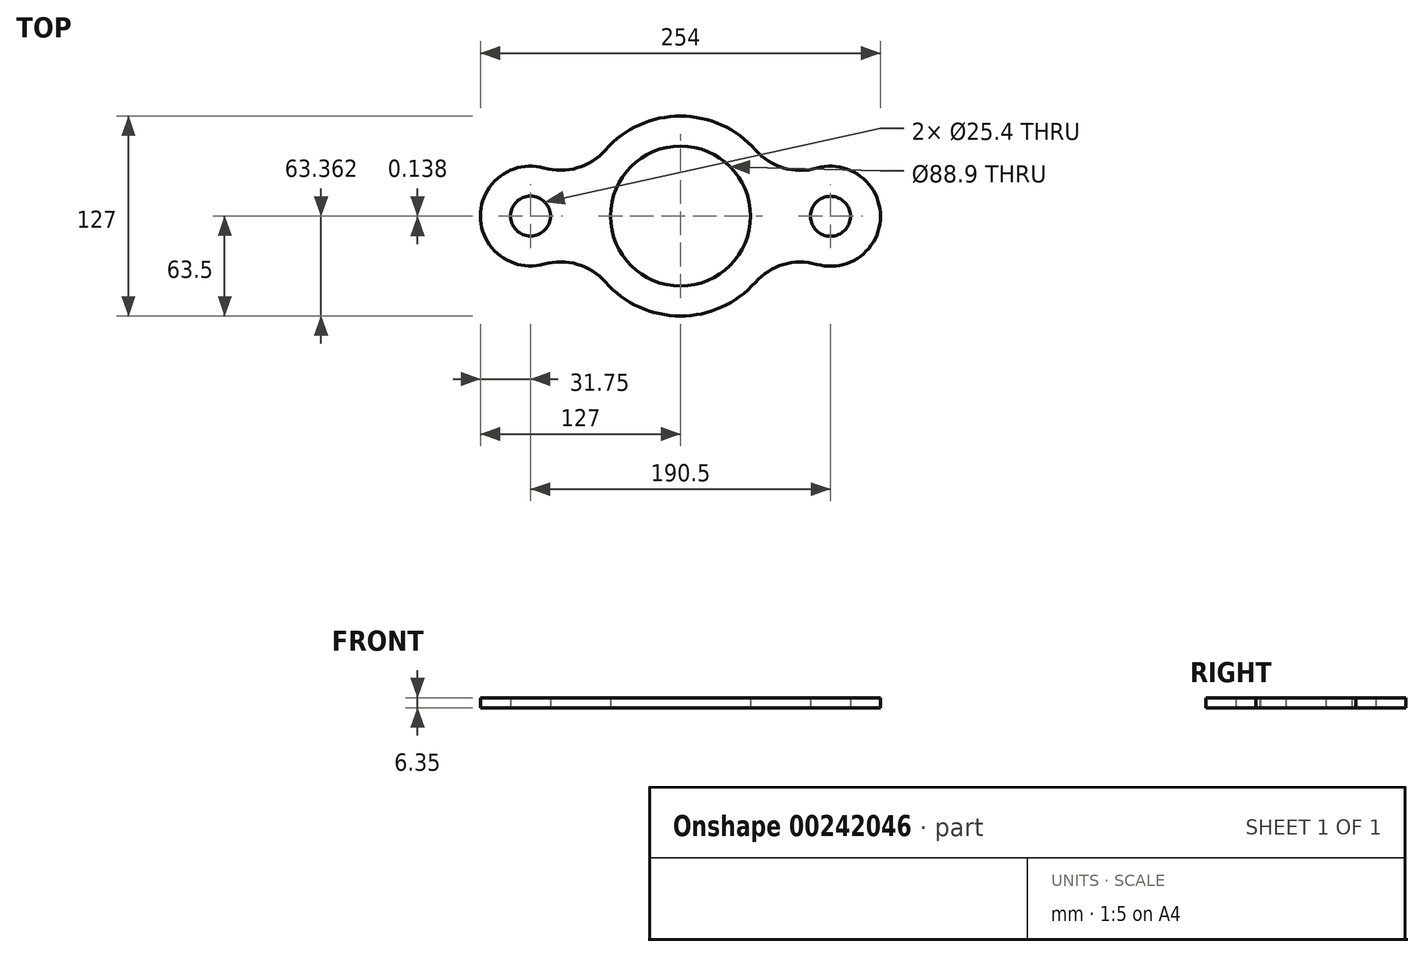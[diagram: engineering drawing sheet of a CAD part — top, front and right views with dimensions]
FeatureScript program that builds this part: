
annotation { "Feature Type Name" : "Feature", "Feature Type Description" : "" }
export const myFeature = defineFeature(function(context is Context, id is Id, definition is map)
    precondition{}
    {
        {
            var Q0;
            Q0=qCreatedBy(makeId("Top.planeOp"),FACE);
            var sketch = newSketch(context, id + "F0", { "sketchPlane" : qUnion([Q0])});
            skArc(sketch, "E0", {"start": v(-47.62, -42) * mm, "mid": v(-0.05, -63.5) * mm, "end": v(47.56, -42.07) * mm});
            skCircle(sketch, "E1", {"center": v(0, 0) * mm, "radius": 44.45 * mm});
            skArc(sketch, "E2", {"start": v(-86.6, 30.55) * mm, "mid": v(-127, 0) * mm, "end": v(-86.6, -30.55) * mm});
            skCircle(sketch, "E3", {"center": v(-95.25, 0) * mm, "radius": 12.7 * mm});
            skArc(sketch, "E4", {"start": v(86.55, -30.67) * mm, "mid": v(127, -0.18) * mm, "end": v(86.64, 30.42) * mm});
            skCircle(sketch, "E5", {"center": v(95.25, -0.14) * mm, "radius": 12.7 * mm});
            skArc(sketch, "E6", {"start": v(47.69, 41.93) * mm, "mid": v(65.5, 30.55) * mm, "end": v(86.64, 30.42) * mm});
            skArc(sketch, "E7", {"start": v(-86.6, 30.55) * mm, "mid": v(-65.45, 30.65) * mm, "end": v(-47.62, 42) * mm});
            skArc(sketch, "E8", {"start": v(86.55, -30.67) * mm, "mid": v(65.4, -30.74) * mm, "end": v(47.56, -42.07) * mm});
            skArc(sketch, "E9", {"start": v(-47.62, -42) * mm, "mid": v(-65.45, -30.65) * mm, "end": v(-86.6, -30.55) * mm});
            skArc(sketch, "E10.trimOffspring", {"start": v(47.69, 41.93) * mm, "mid": v(0.05, 63.5) * mm, "end": v(-47.62, 42) * mm});
            skSolve(sketch);
        }
        {
            var Q0;
            Q0=makeQuery(id+"F0.imprint","IMPRINT",FACE,{"disambiguationData":[TD([[makeQuery(id+"F0.imprint","IMPRINT",EDGE,{"derivedFrom":sQuery(id+"F0.wireOp",EDGE,"E0")}),1.0]])]});
            extrude(context, id + "F1", {"entities" : qUnion([Q0]), "depth" : 6.35 * mm});
        }
    });
